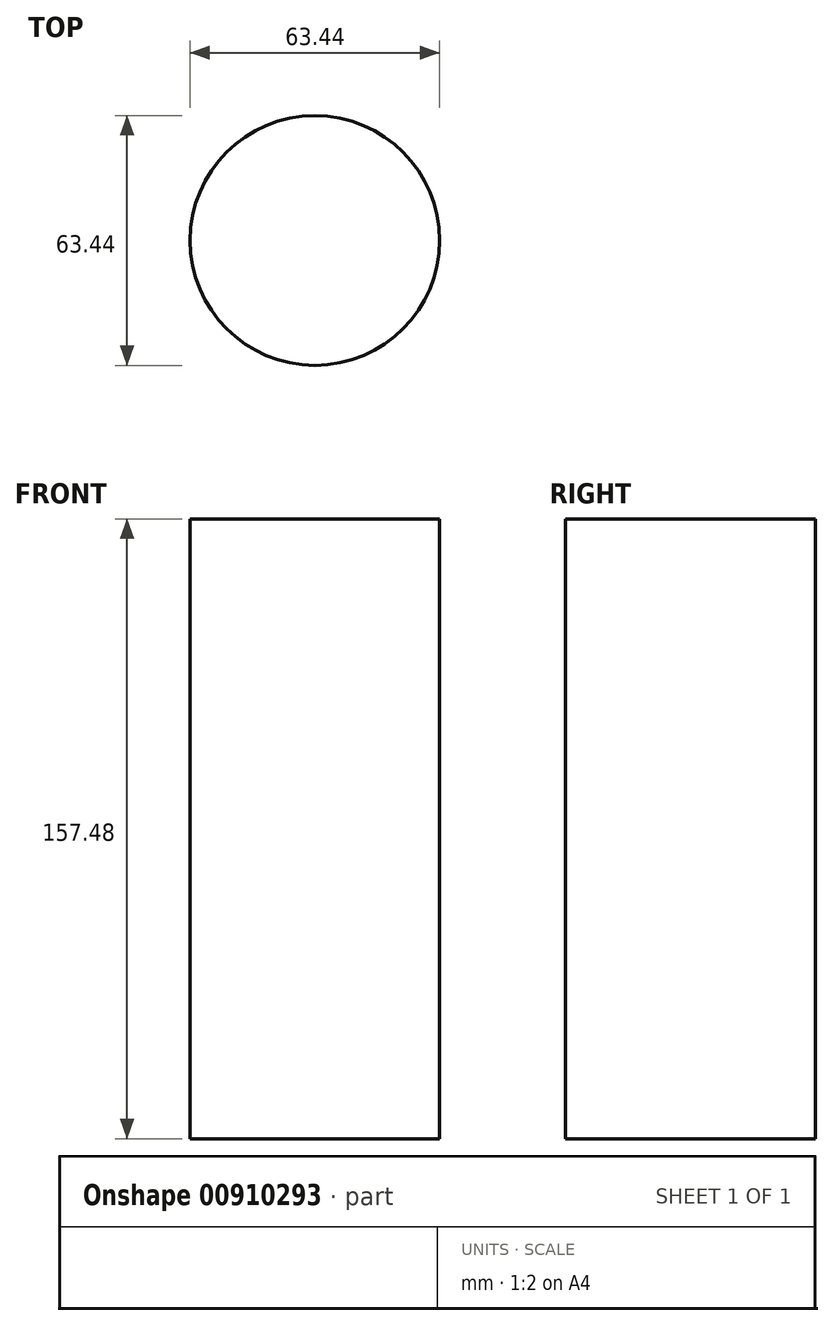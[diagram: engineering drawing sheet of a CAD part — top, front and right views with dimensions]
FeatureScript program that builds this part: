
annotation { "Feature Type Name" : "Feature", "Feature Type Description" : "" }
export const myFeature = defineFeature(function(context is Context, id is Id, definition is map)
    precondition{}
    {
        {
            var Q0;
            Q0=qCreatedBy(makeId("Top.planeOp"),FACE);
            var sketch = newSketch(context, id + "F0", { "sketchPlane" : qUnion([Q0])});
            skCircle(sketch, "E0", {"center": v(0, 0) * mm, "radius": 31.72 * mm});
            skSolve(sketch);
        }
        {
            var Q0;
            Q0=makeQuery(id+"F0.imprint","IMPRINT",FACE,{"disambiguationData":[TD([[makeQuery(id+"F0.imprint","IMPRINT",EDGE,{"derivedFrom":sQuery(id+"F0.wireOp",EDGE,"E0")}),1.0]])]});
            var sketch = newSketch(context, id + "F1", { "sketchPlane" : qUnion([Q0])});
            skSolve(sketch);
        }
        {
            var Q0;
            Q0=makeQuery(id+"F0.imprint","IMPRINT",FACE,{"disambiguationData":[TD([[makeQuery(id+"F0.imprint","IMPRINT",EDGE,{"derivedFrom":sQuery(id+"F0.wireOp",EDGE,"E0")}),1.0]])]});
            extrude(context, id + "F2", {"entities" : qUnion([Q0]), "depth" : -78.74 * mm, "offsetDistance" : 25.4 * mm});
        }
        {
            var Q0;
            Q0=makeQuery(id+"F1.imprint","IMPRINT",FACE,{"disambiguationData":[TD([[makeQuery(id+"F1.imprint","IMPRINT",EDGE,{"derivedFrom":makeQuery(id+"F0.imprint","IMPRINT",EDGE,{"derivedFrom":sQuery(id+"F0.wireOp",EDGE,"E0")})}),1.0]])]});
            extrude(context, id + "F3", {"entities" : qUnion([Q0]), "operationType" : NewBodyOperationType.ADD, "depth" : 78.74 * mm, "offsetDistance" : 25.4 * mm});
        }
    });
